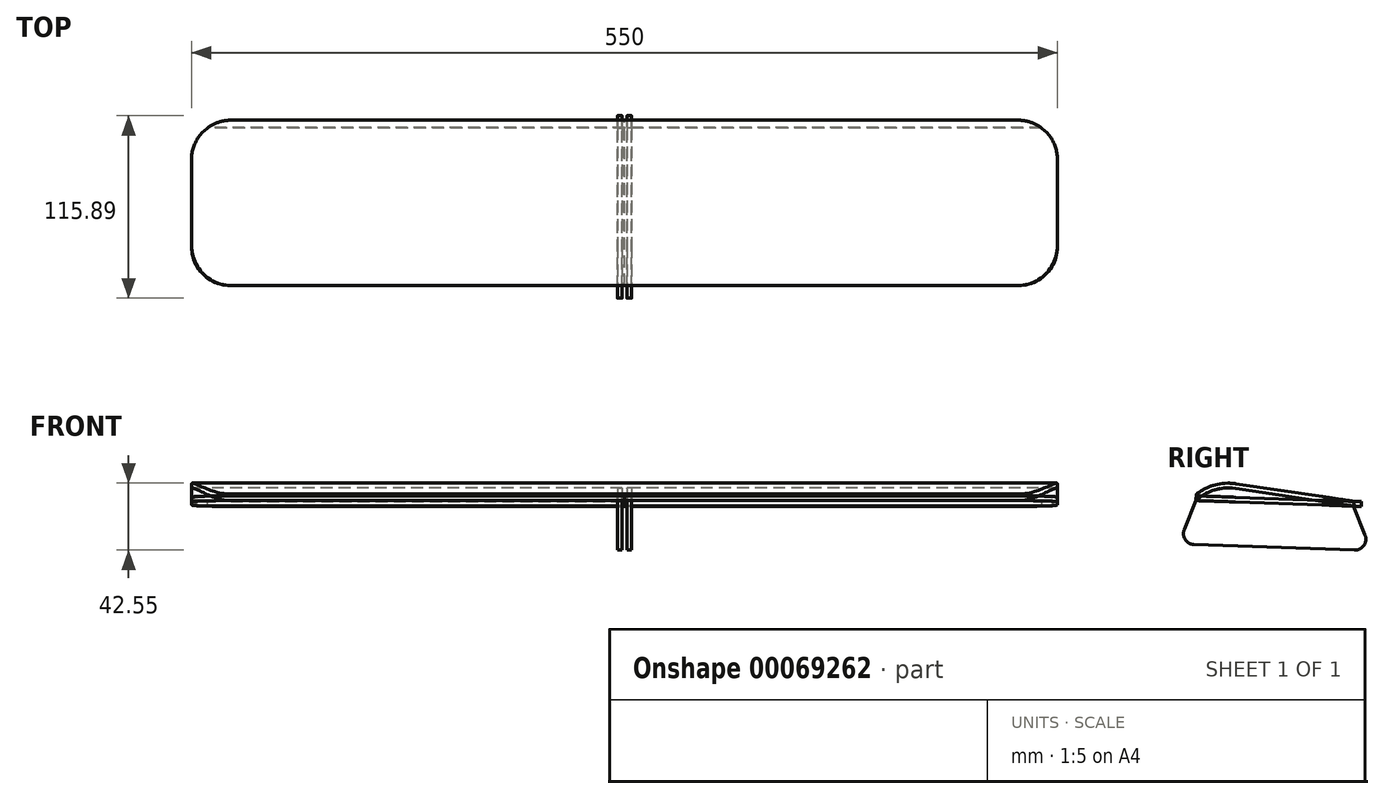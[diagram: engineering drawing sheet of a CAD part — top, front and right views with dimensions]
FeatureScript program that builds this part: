
annotation { "Feature Type Name" : "Feature", "Feature Type Description" : "" }
export const myFeature = defineFeature(function(context is Context, id is Id, definition is map)
    precondition{}
    {
        {
            assignVariable(context, id + "F0", {"name" : "foam_w", "anyValue" : 3 * mm});
        }
        {
            var Q0;
            Q0=qCreatedBy(makeId("Right.planeOp"),FACE);
            var sketch = newSketch(context, id + "F1", { "sketchPlane" : qUnion([Q0])});
            skLineSegment(sketch, "E0", {"start": v(0, -9.84) * mm, "end": v(0, -3) * mm});
            skLineSegment(sketch, "E1", {"start": v(10.31, 24.68) * mm, "end": v(45.98, 23.56) * mm});
            skLineSegment(sketch, "E2", {"start": v(0, 0) * mm, "end": v(320, 0) * mm});
            skLineSegment(sketch, "E3", {"start": v(65, 47.7) * mm, "end": v(164.94, 44.22) * mm});
            skLineSegment(sketch, "E4", {"start": v(171.76, 27.38) * mm, "end": v(164.94, 44.22) * mm});
            skLineSegment(sketch, "E5", {"start": v(320, 15) * mm, "end": v(320, 100) * mm});
            skLineSegment(sketch, "E6", {"start": v(320, 100) * mm, "end": v(330, 100) * mm});
            skLineSegment(sketch, "E7", {"start": v(350, 80) * mm, "end": v(350, 32.17) * mm});
            skLineSegment(sketch, "E8", {"start": v(350, 0) * mm, "end": v(320, 0) * mm, "construction": true});
            skLineSegment(sketch, "E9", {"start": v(320, 100) * mm, "end": v(319.9, 100) * mm});
            skLineSegment(sketch, "E10", {"start": v(300.74, 85.72) * mm, "end": v(286.6, 38.38) * mm});
            skLineSegment(sketch, "E11", {"start": v(164.94, 44.22) * mm, "end": v(63.57, 44.22) * mm, "construction": true});
            skLineSegment(sketch, "E12", {"start": v(0, 0) * mm, "end": v(0, 10) * mm, "construction": true});
            skLineSegment(sketch, "E13", {"start": v(10.16, -19.84) * mm, "end": v(310.16, -15.15) * mm});
            skLineSegment(sketch, "E14", {"start": v(320, -5.16) * mm, "end": v(320, 15) * mm});
            skLineSegment(sketch, "E15", {"start": v(350, -0.21) * mm, "end": v(350, 0) * mm});
            skPoint(sketch, "E16", {"position": v(114.97, 45.96) * mm});
            skLineSegment(sketch, "E17", {"start": v(65, 47.7) * mm, "end": v(58.42, 31.63) * mm});
            skPoint(sketch, "E18.visualSharp", {"position": v(350, 100) * mm});
            skArc(sketch, "E18.filletArc", {"start": v(350, 80) * mm, "mid": v(344.14, 94.14) * mm, "end": v(330, 100) * mm});
            skPoint(sketch, "E19.visualSharp", {"position": v(305, 100) * mm});
            skArc(sketch, "E19.filletArc", {"start": v(319.9, 100) * mm, "mid": v(307.95, 96.04) * mm, "end": v(300.74, 85.72) * mm});
            skPoint(sketch, "E20.visualSharp", {"position": v(0, 25) * mm});
            skArc(sketch, "E20.filletArc", {"start": v(10.31, 24.68) * mm, "mid": v(3.04, 21.86) * mm, "end": v(0, 14.68) * mm});
            skPoint(sketch, "E21.visualSharp", {"position": v(0, -20) * mm});
            skArc(sketch, "E21.filletArc", {"start": v(0, -9.84) * mm, "mid": v(2.98, -16.97) * mm, "end": v(10.16, -19.84) * mm});
            skArc(sketch, "E22", {"start": v(171.76, 27.38) * mm, "mid": v(176.38, 21.6) * mm, "end": v(183.4, 19.27) * mm});
            skArc(sketch, "E23", {"start": v(256.92, 16.97) * mm, "mid": v(275.4, 22.62) * mm, "end": v(286.6, 38.38) * mm});
            skArc(sketch, "E24", {"start": v(45.98, 23.56) * mm, "mid": v(53.46, 25.65) * mm, "end": v(58.42, 31.63) * mm});
            skLineSegment(sketch, "E25", {"start": v(0, 10) * mm, "end": v(25, 10) * mm});
            skLineSegment(sketch, "E26", {"start": v(25, 10) * mm, "end": v(25, 0) * mm});
            skLineSegment(sketch, "E27", {"start": v(0, 10) * mm, "end": v(0, 14.68) * mm});
            skLineSegment(sketch, "E28", {"start": v(256.92, 16.97) * mm, "end": v(320, 15) * mm, "construction": true});
            skLineSegment(sketch, "E29", {"start": v(183.4, 19.27) * mm, "end": v(256.92, 16.97) * mm});
            skLineSegment(sketch, "E30", {"start": v(45.98, 23.56) * mm, "end": v(183.4, 19.27) * mm, "construction": true});
            skLineSegment(sketch, "E31", {"start": v(58.42, 31.63) * mm, "end": v(55, 23.28) * mm, "construction": true});
            skLineSegment(sketch, "E32", {"start": v(174.94, 19.53) * mm, "end": v(171.76, 27.38) * mm, "construction": true});
            skLineSegment(sketch, "E33", {"start": v(286.6, 38.38) * mm, "end": v(280, 16.25) * mm, "construction": true});
            skLineSegment(sketch, "E34", {"start": v(320, -3) * mm, "end": v(0, -3) * mm});
            skPoint(sketch, "E34.endSnap0", {"position": v(0, -3) * mm});
            skLineSegment(sketch, "E35", {"start": v(0, -3) * mm, "end": v(0, 0) * mm, "construction": true});
            skLineSegment(sketch, "E36", {"start": v(56.13, 26.05) * mm, "end": v(173.96, 21.94) * mm, "construction": true});
            skLineSegment(sketch, "E37", {"start": v(164.94, 44.22) * mm, "end": v(164.17, 22.28) * mm, "construction": true});
            skLineSegment(sketch, "E38", {"start": v(173.96, 21.94) * mm, "end": v(173.2, 0) * mm, "construction": true});
            skLineSegment(sketch, "E39.0", {"start": v(53.71, 20.13) * mm, "end": v(173.76, 15.94) * mm, "construction": true});
            skPoint(sketch, "E40.visualSharp", {"position": v(320, -15) * mm});
            skArc(sketch, "E40.filletArc", {"start": v(310.16, -15.15) * mm, "mid": v(317.13, -12.17) * mm, "end": v(320, -5.16) * mm});
            skLineSegment(sketch, "E41", {"start": v(320, 0) * mm, "end": v(344.64, 20.68) * mm});
            skPoint(sketch, "E42.visualSharp", {"position": v(350, 25.17) * mm});
            skArc(sketch, "E42.filletArc", {"start": v(344.64, 20.68) * mm, "mid": v(348.6, 25.83) * mm, "end": v(350, 32.17) * mm});
            skPoint(sketch, "E43", {"position": v(115.04, 30) * mm});
            skLineSegment(sketch, "E44", {"start": v(58.55, 31.97) * mm, "end": v(171.52, 28.03) * mm});
            skSolve(sketch);
        }
        {
            var Q0;
            Q0=qCreatedBy(makeId("Right.planeOp"),FACE);
            var sketch = newSketch(context, id + "F2", { "sketchPlane" : qUnion([Q0])});
            skPoint(sketch, "E45.0", {"position": v(65, 47.7) * mm});
            skPoint(sketch, "E45.1", {"position": v(164.94, 44.22) * mm});
            skLineSegment(sketch, "E46", {"start": v(164.94, 44.22) * mm, "end": v(89.9, 55.44) * mm});
            skArc(sketch, "E47", {"start": v(89.9, 55.44) * mm, "mid": v(76.56, 54.42) * mm, "end": v(65, 47.7) * mm});
            skLineSegment(sketch, "E48", {"start": v(65, 47.7) * mm, "end": v(75.58, 57.58) * mm, "construction": true});
            skArc(sketch, "E49.0", {"start": v(90.34, 58.4) * mm, "mid": v(75.67, 57.28) * mm, "end": v(62.95, 49.9) * mm});
            skLineSegment(sketch, "E49.1", {"start": v(165.38, 47.19) * mm, "end": v(90.34, 58.4) * mm});
            skLineSegment(sketch, "E50", {"start": v(165.38, 47.19) * mm, "end": v(164.94, 44.22) * mm});
            skLineSegment(sketch, "E51", {"start": v(62.95, 49.9) * mm, "end": v(65, 47.7) * mm});
            skLineSegment(sketch, "E52", {"start": v(65, 47.7) * mm, "end": v(57.52, 29.43) * mm});
            skLineSegment(sketch, "E53", {"start": v(63.75, 19.78) * mm, "end": v(165.65, 16.23) * mm});
            skLineSegment(sketch, "E54", {"start": v(172.38, 25.85) * mm, "end": v(164.94, 44.22) * mm});
            skLineSegment(sketch, "E55.0", {"start": v(65, 47.7) * mm, "end": v(164.94, 44.22) * mm, "construction": true});
            skPoint(sketch, "E56.visualSharp", {"position": v(53.71, 20.13) * mm});
            skArc(sketch, "E56.filletArc", {"start": v(57.52, 29.43) * mm, "mid": v(58.12, 22.98) * mm, "end": v(63.75, 19.78) * mm});
            skPoint(sketch, "E57.visualSharp", {"position": v(176.43, 15.85) * mm});
            skArc(sketch, "E57.filletArc", {"start": v(165.65, 16.23) * mm, "mid": v(171.63, 19.2) * mm, "end": v(172.38, 25.85) * mm});
            skSolve(sketch);
        }
        {
            var Q0;
            Q0=qCreatedBy(makeId("Top.planeOp"),FACE);
            var sketch = newSketch(context, id + "F3", { "sketchPlane" : qUnion([Q0])});
            skPoint(sketch, "E58.0", {"position": v(0, 350) * mm});
            skPoint(sketch, "E58.1", {"position": v(0, 320) * mm});
            skLineSegment(sketch, "E59", {"start": v(0, 0) * mm, "end": v(0, 320) * mm});
            skLineSegment(sketch, "E60", {"start": v(0, 320) * mm, "end": v(-110, 320) * mm});
            skLineSegment(sketch, "E61", {"start": v(-110, 320) * mm, "end": v(-110, 311.18) * mm});
            skLineSegment(sketch, "E62", {"start": v(-94.18, 291.62) * mm, "end": v(-40.9, 280.24) * mm});
            skLineSegment(sketch, "E63", {"start": v(0, 0) * mm, "end": v(-9.52, 0) * mm});
            skLineSegment(sketch, "E64", {"start": v(-24.52, 15.47) * mm, "end": v(-17.19, 249.96) * mm});
            skLineSegment(sketch, "E65", {"start": v(-110, 320) * mm, "end": v(-110, 330) * mm});
            skLineSegment(sketch, "E66", {"start": v(-90, 350) * mm, "end": v(-41.28, 350) * mm});
            skPoint(sketch, "E67.visualSharp", {"position": v(-110, 295) * mm});
            skArc(sketch, "E67.filletArc", {"start": v(-110, 311.18) * mm, "mid": v(-105.55, 298.6) * mm, "end": v(-94.18, 291.62) * mm});
            skPoint(sketch, "E68.visualSharp", {"position": v(-110, 350) * mm});
            skArc(sketch, "E68.filletArc", {"start": v(-90, 350) * mm, "mid": v(-104.14, 344.14) * mm, "end": v(-110, 330) * mm});
            skArc(sketch, "E69.filletArc", {"start": v(-27.14, 344.14) * mm, "mid": v(-33.63, 348.48) * mm, "end": v(-41.28, 350) * mm});
            skArc(sketch, "E70", {"start": v(-17.19, 249.96) * mm, "mid": v(-23.56, 269.4) * mm, "end": v(-40.9, 280.24) * mm});
            skLineSegment(sketch, "E71", {"start": v(-17.19, 249.96) * mm, "end": v(-15, 320) * mm, "construction": true});
            skLineSegment(sketch, "E72", {"start": v(-40.9, 280.24) * mm, "end": v(-16.4, 275) * mm, "construction": true});
            skPoint(sketch, "E73.visualSharp", {"position": v(-25, 0) * mm});
            skArc(sketch, "E73.filletArc", {"start": v(-24.52, 15.47) * mm, "mid": v(-20.3, 4.56) * mm, "end": v(-9.52, 0) * mm});
            skLineSegment(sketch, "E74.MirrorCS", {"start": v(0, 0) * mm, "end": v(9.52, 0) * mm});
            skArc(sketch, "E75.MirrorCS", {"start": v(24.52, 15.47) * mm, "mid": v(20.3, 4.56) * mm, "end": v(9.52, 0) * mm});
            skLineSegment(sketch, "E76.MirrorCS", {"start": v(24.52, 15.47) * mm, "end": v(17.19, 249.96) * mm});
            skArc(sketch, "E77.MirrorCS", {"start": v(17.19, 249.96) * mm, "mid": v(23.56, 269.4) * mm, "end": v(40.9, 280.24) * mm});
            skLineSegment(sketch, "E78.MirrorCS", {"start": v(94.18, 291.62) * mm, "end": v(40.9, 280.24) * mm});
            skArc(sketch, "E79.MirrorCS", {"start": v(110, 311.18) * mm, "mid": v(105.55, 298.6) * mm, "end": v(94.18, 291.62) * mm});
            skLineSegment(sketch, "E80.MirrorCS", {"start": v(0, 320) * mm, "end": v(110, 320) * mm});
            skLineSegment(sketch, "E81.MirrorCS", {"start": v(90, 350) * mm, "end": v(41.28, 350) * mm});
            skArc(sketch, "E82.MirrorCS", {"start": v(90, 350) * mm, "mid": v(104.14, 344.14) * mm, "end": v(110, 330) * mm});
            skLineSegment(sketch, "E83.MirrorCS", {"start": v(110, 320) * mm, "end": v(110, 330) * mm});
            skLineSegment(sketch, "E84.MirrorCS", {"start": v(110, 320) * mm, "end": v(110, 311.18) * mm});
            skArc(sketch, "E85.MirrorCS", {"start": v(27.14, 344.14) * mm, "mid": v(33.63, 348.48) * mm, "end": v(41.28, 350) * mm});
            skLineSegment(sketch, "E86", {"start": v(-3, 320) * mm, "end": v(-27.14, 344.14) * mm});
            skLineSegment(sketch, "E87.MirrorCS", {"start": v(3, 320) * mm, "end": v(27.14, 344.14) * mm});
            skLineSegment(sketch, "E88", {"start": v(-41.28, 350) * mm, "end": v(41.28, 350) * mm});
            skSolve(sketch);
        }
        {
            var Q0;
            Q0=sQuery(id+"F1.wireOp",EDGE,"E3");
            cPlane(context, id + "F4", {"entities" : qUnion([Q0]), "cplaneType" : CPlaneType.LINE_ANGLE, "offset" : 150 * mm, "angle" : 0 * degree, "width" : 150 * mm, "height" : 150 * mm});
        }
        {
            var Q0;
            Q0=qCreatedBy(id+"F4.planeOp",FACE);
            var sketch = newSketch(context, id + "F5", { "sketchPlane" : qUnion([Q0])});
            skLineSegment(sketch, "E89", {"start": v(0, 63.3) * mm, "end": v(0, 168.3) * mm});
            skLineSegment(sketch, "E90", {"start": v(0, 63.3) * mm, "end": v(-250, 63.3) * mm});
            skLineSegment(sketch, "E91", {"start": v(-275, 88.3) * mm, "end": v(-275, 143.3) * mm});
            skLineSegment(sketch, "E92", {"start": v(-250, 168.3) * mm, "end": v(0, 168.3) * mm});
            skPoint(sketch, "E93.visualSharp", {"position": v(-275, 63.3) * mm});
            skArc(sketch, "E93.filletArc", {"start": v(-275, 88.3) * mm, "mid": v(-267.68, 70.62) * mm, "end": v(-250, 63.3) * mm});
            skPoint(sketch, "E94.visualSharp", {"position": v(-275, 168.3) * mm});
            skArc(sketch, "E94.filletArc", {"start": v(-250, 168.3) * mm, "mid": v(-267.68, 160.97) * mm, "end": v(-275, 143.3) * mm});
            skLineSegment(sketch, "E95.MirrorCS", {"start": v(0, 63.3) * mm, "end": v(250, 63.3) * mm});
            skLineSegment(sketch, "E96.MirrorCS", {"start": v(250, 168.3) * mm, "end": v(0, 168.3) * mm});
            skArc(sketch, "E97.MirrorCS", {"start": v(250, 168.3) * mm, "mid": v(267.68, 160.97) * mm, "end": v(275, 143.3) * mm});
            skLineSegment(sketch, "E98.MirrorCS", {"start": v(275, 88.3) * mm, "end": v(275, 143.3) * mm});
            skArc(sketch, "E99.MirrorCS", {"start": v(275, 88.3) * mm, "mid": v(267.68, 70.62) * mm, "end": v(250, 63.3) * mm});
            skLineSegment(sketch, "E100", {"start": v(0, 103.3) * mm, "end": v(-275, 103.3) * mm});
            skLineSegment(sketch, "E101.MirrorCS", {"start": v(0, 103.3) * mm, "end": v(275, 103.3) * mm});
            skSolve(sketch);
        }
        {
            var Q0;
            Q0=makeQuery(id+"F1.imprint","IMPRINT",FACE,{"disambiguationData":[TD([[makeQuery(id+"F1.imprint","IMPRINT",EDGE,{"derivedFrom":sQuery(id+"F1.wireOp",EDGE,"E1")}),-1.0]])]});
            extrude(context, id + "F6", {"entities" : qUnion([Q0]), "endBound" : BoundingType.SYMMETRIC, "depth" : getVariable(context, 'foam_w')});
        }
        {
            var Q0;
            {var subQ5=sQuery(id+"F1.wireOp",EDGE,"E0");Q0=makeQuery(id+"F1.imprint","IMPRINT",FACE,{"disambiguationData":[TD([[makeQuery(id+"F1.imprint","IMPRINT",EDGE,{"derivedFrom":subQ5}),-1.0]])]});}
            extrude(context, id + "F7", {"entities" : qUnion([Q0]), "endBound" : BoundingType.SYMMETRIC, "depth" : getVariable(context, 'foam_w')});
        }
        {
            var Q0;
            {var subQ3=sQuery(id+"F1.wireOp",EDGE,"E5");Q0=makeQuery(id+"F1.imprint","IMPRINT",FACE,{"disambiguationData":[TD([[makeQuery(id+"F1.imprint","IMPRINT",EDGE,{"derivedFrom":subQ3}),-1.0]])]});}
            extrude(context, id + "F8", {"entities" : qUnion([Q0]), "endBound" : BoundingType.SYMMETRIC, "depth" : getVariable(context, 'foam_w')});
        }
        {
            var Q0;
            Q0=makeQuery(id+"F3.imprint","IMPRINT",FACE,{"disambiguationData":[TD([[makeQuery(id+"F3.imprint","IMPRINT",EDGE,{"derivedFrom":sQuery(id+"F3.wireOp",EDGE,"E59")}),-1.0]])]});
            var Q1;
            Q1=makeQuery(id+"F3.imprint","IMPRINT",FACE,{"disambiguationData":[TD([[makeQuery(id+"F3.imprint","IMPRINT",EDGE,{"derivedFrom":sQuery(id+"F3.wireOp",EDGE,"E59")}),1.0]])]});
            extrude(context, id + "F9", {"entities" : qUnion([Q0, Q1]), "oppositeDirection" : true, "depth" : getVariable(context, 'foam_w')});
        }
        {
            var Q0;
            Q0=makeQuery(id+"F3.imprint","IMPRINT",FACE,{"disambiguationData":[TD([[makeQuery(id+"F3.imprint","IMPRINT",EDGE,{"derivedFrom":sQuery(id+"F3.wireOp",EDGE,"E80.MirrorCS")}),1.0]])]});
            var Q1;
            Q1=makeQuery(id+"F3.imprint","IMPRINT",FACE,{"disambiguationData":[TD([[makeQuery(id+"F3.imprint","IMPRINT",EDGE,{"derivedFrom":sQuery(id+"F3.wireOp",EDGE,"E60")}),-1.0]])]});
            var Q2;
            Q2=makeQuery(id+"F3.imprint","IMPRINT",FACE,{"disambiguationData":[TD([[makeQuery(id+"F3.imprint","IMPRINT",EDGE,{"derivedFrom":sQuery(id+"F3.wireOp",EDGE,"E69.filletArc")}),-1.0]])]});
            extrude(context, id + "F10", {"entities" : qUnion([Q0, Q1, Q2]), "oppositeDirection" : true, "depth" : getVariable(context, 'foam_w')});
        }
        {
            var Q0;
            Q0=makeQuery(id+"F2.imprint","IMPRINT",FACE,{"disambiguationData":[TD([[makeQuery(id+"F2.imprint","IMPRINT",EDGE,{"derivedFrom":sQuery(id+"F2.wireOp",EDGE,"E46")}),-1.0]])]});
            extrude(context, id + "F11", {"entities" : qUnion([Q0]), "endBound" : BoundingType.SYMMETRIC, "depth" : 800 * mm});
        }
        {
            var Q0;
            {var subQ0=sQuery(id+"F5.wireOp",EDGE,"E95.MirrorCS");Q0=makeQuery(id+"F5.imprint","IMPRINT",FACE,{"disambiguationData":[TD([[makeQuery(id+"F5.imprint","IMPRINT",EDGE,{"derivedFrom":subQ0}),1.0]])]});}
            var Q1;
            {var subQ0=sQuery(id+"F5.wireOp",EDGE,"E96.MirrorCS");Q1=makeQuery(id+"F5.imprint","IMPRINT",FACE,{"disambiguationData":[TD([[makeQuery(id+"F5.imprint","IMPRINT",EDGE,{"derivedFrom":subQ0}),1.0]])]});}
            var Q2;
            Q2=makeQuery(id+"F5.imprint","IMPRINT",FACE,{"disambiguationData":[TD([[makeQuery(id+"F5.imprint","IMPRINT",EDGE,{"derivedFrom":sQuery(id+"F5.wireOp",EDGE,"E91")}),-1.0]])]});
            var Q3;
            {var subQ0=sQuery(id+"F5.wireOp",EDGE,"E90");Q3=makeQuery(id+"F5.imprint","IMPRINT",FACE,{"disambiguationData":[TD([[makeQuery(id+"F5.imprint","IMPRINT",EDGE,{"derivedFrom":subQ0}),-1.0]])]});}
            extrude(context, id + "F12", {"entities" : qUnion([Q0, Q1, Q2, Q3]), "operationType" : NewBodyOperationType.INTERSECT, "depth" : 25 * mm});
        }
        {
            var Q0;
            Q0=makeQuery(id+"F2.imprint","IMPRINT",FACE,{"disambiguationData":[TD([[makeQuery(id+"F2.imprint","IMPRINT",EDGE,{"derivedFrom":sQuery(id+"F2.wireOp",EDGE,"E46")}),1.0]])]});
            extrude(context, id + "F13", {"entities" : qUnion([Q0]), "depth" : getVariable(context, 'foam_w') + getVariable(context, 'foam_w') / 2, "hasSecondDirection" : true, "secondDirectionOppositeDirection" : false, "secondDirectionDepth" : getVariable(context, 'foam_w') / 2});
        }
        {
            var Q0;
            Q0=makeQuery(id+"F13.opExtrude","SWEPT_BODY",BODY,{"disambiguationData":[OSD([sQuery(id+"F2.wireOp",EDGE,"E46"),sQuery(id+"F2.wireOp",EDGE,"E47"),sQuery(id+"F2.wireOp",EDGE,"E52"),sQuery(id+"F2.wireOp",EDGE,"E53"),sQuery(id+"F2.wireOp",EDGE,"E54")])]});
            var Q1;
            Q1=qCreatedBy(makeId("Right.planeOp"),FACE);
            mirror(context, id + "F14", {"entities" : qUnion([Q0]), "mirrorPlane" : qUnion([Q1])});
        }
        {
            var Q0;
            Q0=makeQuery(id+"F5.imprint","IMPRINT",FACE,{"disambiguationData":[TD([[makeQuery(id+"F5.imprint","IMPRINT",EDGE,{"derivedFrom":sQuery(id+"F5.wireOp",EDGE,"E89")}),1.0]])]});
            var Q1;
            Q1=makeQuery(id+"F5.imprint","IMPRINT",FACE,{"disambiguationData":[TD([[makeQuery(id+"F5.imprint","IMPRINT",EDGE,{"derivedFrom":sQuery(id+"F5.wireOp",EDGE,"E91")}),-1.0]])]});
            extrude(context, id + "F15", {"entities" : qUnion([Q0, Q1]), "depth" : getVariable(context, 'foam_w')});
        }
        {
            var Q0;
            Q0=makeQuery(id+"F5.imprint","IMPRINT",FACE,{"disambiguationData":[TD([[makeQuery(id+"F5.imprint","IMPRINT",EDGE,{"derivedFrom":sQuery(id+"F5.wireOp",EDGE,"E89")}),-1.0]])]});
            var Q1;
            {var subQ0=sQuery(id+"F5.wireOp",EDGE,"E96.MirrorCS");Q1=makeQuery(id+"F5.imprint","IMPRINT",FACE,{"disambiguationData":[TD([[makeQuery(id+"F5.imprint","IMPRINT",EDGE,{"derivedFrom":subQ0}),1.0]])]});}
            extrude(context, id + "F16", {"entities" : qUnion([Q0, Q1]), "depth" : getVariable(context, 'foam_w')});
        }
    });
